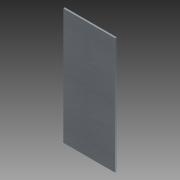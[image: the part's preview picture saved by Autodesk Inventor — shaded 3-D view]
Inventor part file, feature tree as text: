
AUTODESK INVENTOR PART (.ipt)
format: ipt  version: 2011 SP1 (Build 150282100, 282)  size: 74,752 bytes
history: native  units: in
note: dims shown in document units (in); Inventor stores cm internally (conversion verified against a paired STEP export)
features: extrude x1, sketch x1
ambient origin geometry x8: Origin, YZ Plane, XZ Plane, XY Plane, X Axis, Y Axis, Z Axis, Center Point
bodies: Solid1 (feature_tree)
feature tree (2):
  extrude  "Extrusion1"  Depth=9.0in
  sketch  "Sketch1"  dims[d0=4.0in d1=9.0in d2=4.5in d3=2.0in d4=0.125in d5=0.0in]
